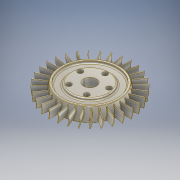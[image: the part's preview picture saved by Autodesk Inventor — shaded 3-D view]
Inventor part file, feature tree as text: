
AUTODESK INVENTOR PART (.ipt)
format: ipt  version: 2019 (Build 230136000, 136)  size: 1,409,024 bytes
history: native  units: mm
features: sketch x7, extrude x6, other x5, fillet x4, pattern_circular x2, hole x1
ambient origin geometry x8: Origin, YZ Plane, XZ Plane, XY Plane, X Axis, Y Axis, Z Axis, Center Point
bodies: Solid1 (feature_tree)
feature tree (25):
  other  "Table"
  other  "Front Compression Fan-01"
  other  "Front Compression Fan-02"
  other  "Front Compression Fan-03"
  other  "Front Compression Fan-04"
  extrude  "Extrusion1"  Depth=30.0mm
  extrude  "Extrusion2"  Depth=1.5mm
  extrude  "Extrusion3"  Depth=30.0mm
  fillet  "Fillet3"  Radius=5.0mm
  pattern_circular  "Circular Pattern1"  Count=8  [1 undecoded]
  extrude  "Extrusion4"  Depth=320.0mm
  hole  "Hole1"  [1 undecoded]
  pattern_circular  "Circular Pattern2"  Count=5 Angle=360.0deg
  extrude  "Extrusion6"  Depth=1.0mm
  fillet  "Fillet2"  Radius=5.0mm
  extrude  "Extrusion7"  Depth=1.0mm
  fillet  "Fillet4"  Radius=1.0mm
  fillet  "Fillet5"  Radius=90.0mm
  sketch  "Sketch1"  dims[d3=-1.745329mm d4=30.0mm]
  sketch  "Sketch2"  dims[d5=15.0mm d6=0.0mm d7=1.5mm]
  sketch  "Sketch3"  dims[d8=30.0mm d9=20.0mm d10=5.0mm d11=80.0mm d12=0.0mm]
  sketch  "Sketch4"  dims[d13=320.0mm d14=360.0deg d17=320.0mm]
  sketch  "Sketch7"  dims[d18=0.0mm d19=-0.872665mm d26=12.0mm]
  sketch  "Sketch8"  dims[d27=35.0mm]
  sketch  "Sketch9"  dims[d28=12.0mm d29=6.0mm d30=4.0mm d31=2.0mm d32=90.0deg d33=8.0mm d34=20.594885mm d35=50.0mm d36=360.0deg d38=90.0mm d40=5.0mm d41=0.0mm d42=3.0mm d43=1.0mm d44=90.0mm d46=5.0mm d47=0.0mm d48=3.0mm d49=1.0mm]
note: 2 required parameter values undecoded (feature->parameter linkage not recoverable at this tier; creation-order binding heuristic only, values carry confidence <= 0.55)
